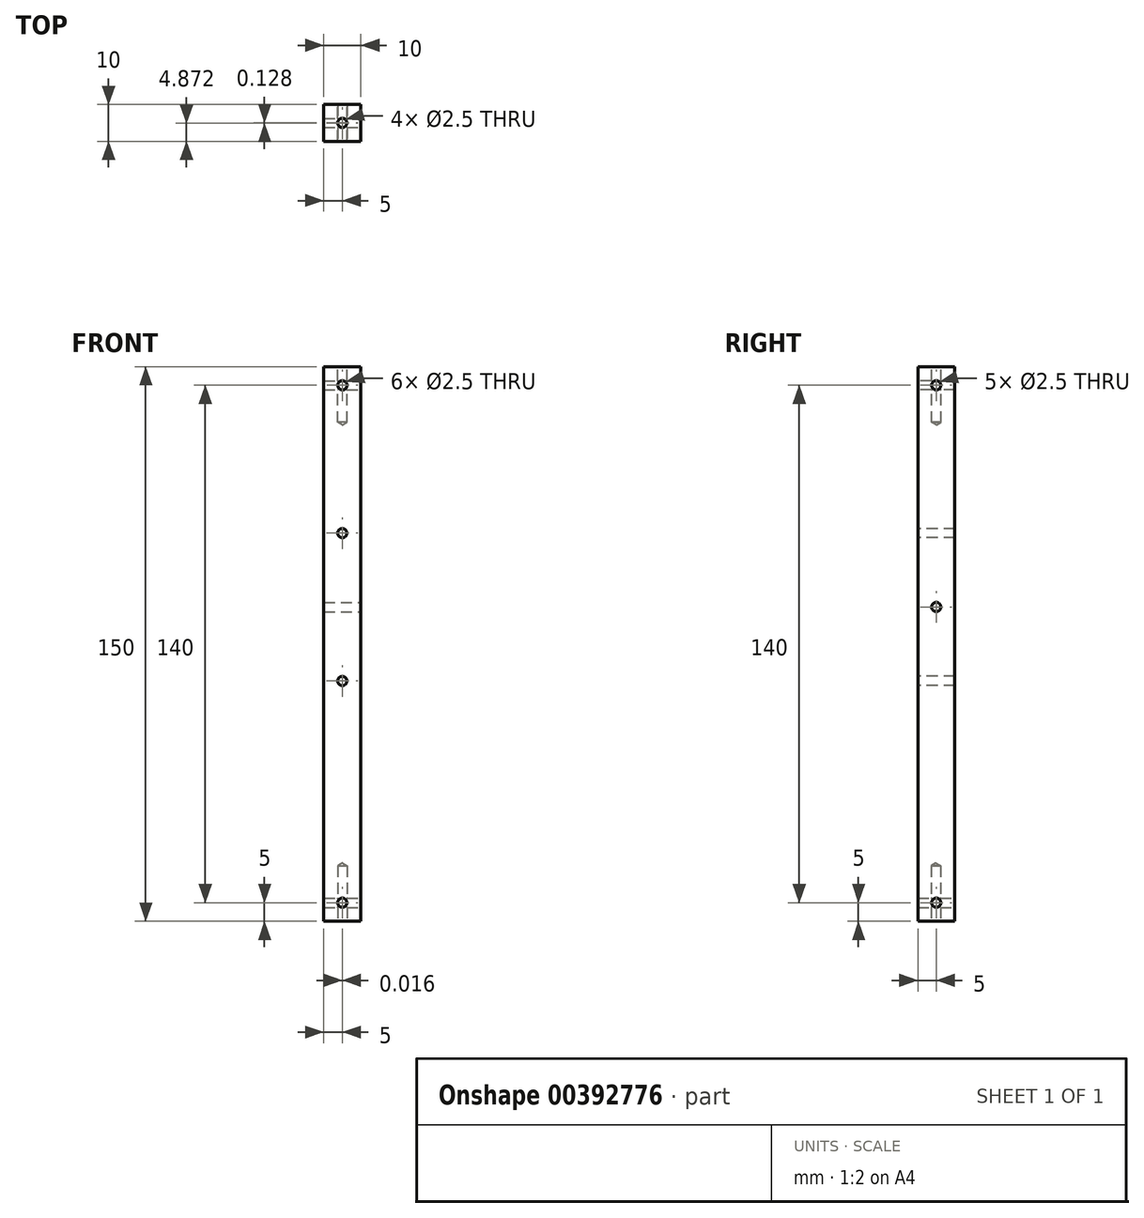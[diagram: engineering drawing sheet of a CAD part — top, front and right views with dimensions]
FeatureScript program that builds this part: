
annotation { "Feature Type Name" : "Feature", "Feature Type Description" : "" }
export const myFeature = defineFeature(function(context is Context, id is Id, definition is map)
    precondition{}
    {
        {
            var Q0;
            Q0=qCreatedBy(makeId("Top.planeOp"),FACE);
            var sketch = newSketch(context, id + "F0", { "sketchPlane" : qUnion([Q0])});
            skLineSegment(sketch, "E0.bottom", {"start": v(0, 0) * mm, "end": v(10, 0) * mm});
            skLineSegment(sketch, "E0.top", {"start": v(0, -10) * mm, "end": v(10, -10) * mm});
            skLineSegment(sketch, "E0.left", {"start": v(0, 0) * mm, "end": v(0, -10) * mm});
            skLineSegment(sketch, "E0.right", {"start": v(10, 0) * mm, "end": v(10, -10) * mm});
            skSolve(sketch);
        }
        {
            var Q0;
            Q0 = qSketchRegion(id + "F0", true);
            extrude(context, id + "F1", {"entities" : qUnion([Q0]), "depth" : 150 * mm});
        }
        {
            var Q0;
            Q0=makeQuery(id+"F1.opExtrude","CAP_FACE",FACE,{"disambiguationData":[OSD([sQuery(id+"F0.wireOp",EDGE,"E0.bottom"),sQuery(id+"F0.wireOp",EDGE,"E0.top"),sQuery(id+"F0.wireOp",EDGE,"E0.left"),sQuery(id+"F0.wireOp",EDGE,"E0.right")])],"isStart":false});
            var sketch = newSketch(context, id + "F2", { "sketchPlane" : qUnion([Q0])});
            skLineSegment(sketch, "E1.bottom", {"start": v(0, -10) * mm, "end": v(5, -10) * mm});
            skLineSegment(sketch, "E1.top", {"start": v(0, -5) * mm, "end": v(5, -5) * mm});
            skLineSegment(sketch, "E1.left", {"start": v(0, -10) * mm, "end": v(0, -5) * mm});
            skLineSegment(sketch, "E1.right", {"start": v(5, -10) * mm, "end": v(5, -5) * mm});
            skSolve(sketch);
        }
        {
            var Q0;
            Q0=sQuery(id+"F2.wireOp",VERTEX,"E1.top.end");
            var Q1;
            Q1=makeQuery(id+"F1.opExtrude","SWEPT_BODY",BODY,{"disambiguationData":[OSD([sQuery(id+"F0.wireOp",EDGE,"E0.bottom"),sQuery(id+"F0.wireOp",EDGE,"E0.top"),sQuery(id+"F0.wireOp",EDGE,"E0.left"),sQuery(id+"F0.wireOp",EDGE,"E0.right")])]});
            hole(context, id + "F3", {"style" : HoleStyle.SIMPLE, "endStyle" : HoleEndStyle.BLIND, "holeDiameter" : 2.5 * mm, "holeDepth" : 15 * mm, "isTappedThrough" : true, "tappedDepth" : 12 * mm, "tapClearance" : 3, "locations" : qUnion([Q0]), "scope" : qUnion([Q1])});
        }
        {
            var Q0;
            Q0=makeQuery(id+"F0.imprint","IMPRINT",FACE,{"disambiguationData":[TD([[makeQuery(id+"F0.imprint","IMPRINT",EDGE,{"derivedFrom":sQuery(id+"F0.wireOp",EDGE,"E0.bottom")}),-1.0]])]});
            var sketch = newSketch(context, id + "F4", { "sketchPlane" : qUnion([Q0])});
            skLineSegment(sketch, "E2.bottom", {"start": v(0, -10.13) * mm, "end": v(5, -10.13) * mm});
            skLineSegment(sketch, "E2.top", {"start": v(0, -5.13) * mm, "end": v(5, -5.13) * mm});
            skLineSegment(sketch, "E2.left", {"start": v(0, -10.13) * mm, "end": v(0, -5.13) * mm});
            skLineSegment(sketch, "E2.right", {"start": v(5, -10.13) * mm, "end": v(5, -5.13) * mm});
            skSolve(sketch);
        }
        {
            var Q0;
            Q0=sQuery(id+"F4.wireOp",VERTEX,"E2.right.end");
            var Q1;
            Q1=makeQuery(id+"F1.opExtrude","SWEPT_BODY",BODY,{"disambiguationData":[OSD([sQuery(id+"F0.wireOp",EDGE,"E0.bottom"),sQuery(id+"F0.wireOp",EDGE,"E0.top"),sQuery(id+"F0.wireOp",EDGE,"E0.left"),sQuery(id+"F0.wireOp",EDGE,"E0.right")])]});
            hole(context, id + "F5", {"style" : HoleStyle.SIMPLE, "endStyle" : HoleEndStyle.BLIND, "oppositeDirection" : true, "holeDiameter" : 2.5 * mm, "holeDepth" : 15 * mm, "isTappedThrough" : true, "tappedDepth" : 12 * mm, "tapClearance" : 3, "locations" : qUnion([Q0]), "scope" : qUnion([Q1])});
        }
        {
            var Q0;
            Q0=makeQuery(id+"F1.opExtrude","SWEPT_FACE",FACE,{"disambiguationData":[OSD([sQuery(id+"F0.wireOp",EDGE,"E0.bottom")])]});
            var sketch = newSketch(context, id + "F6", { "sketchPlane" : qUnion([Q0])});
            skLineSegment(sketch, "E3.bottom", {"start": v(-10, 0) * mm, "end": v(-5, 0) * mm});
            skLineSegment(sketch, "E3.top", {"start": v(-10, 5) * mm, "end": v(-5, 5) * mm});
            skLineSegment(sketch, "E3.left", {"start": v(-10, 0) * mm, "end": v(-10, 5) * mm});
            skLineSegment(sketch, "E3.right", {"start": v(-5, 0) * mm, "end": v(-5, 5) * mm});
            skSolve(sketch);
        }
        {
            var Q0;
            Q0=sQuery(id+"F6.wireOp",VERTEX,"E3.right.end");
            var Q1;
            Q1=makeQuery(id+"F1.opExtrude","SWEPT_BODY",BODY,{"disambiguationData":[OSD([sQuery(id+"F0.wireOp",EDGE,"E0.bottom"),sQuery(id+"F0.wireOp",EDGE,"E0.top"),sQuery(id+"F0.wireOp",EDGE,"E0.left"),sQuery(id+"F0.wireOp",EDGE,"E0.right")])]});
            hole(context, id + "F7", {"style" : HoleStyle.SIMPLE, "endStyle" : HoleEndStyle.BLIND, "holeDiameter" : 2.5 * mm, "holeDepth" : 10 * mm, "isTappedThrough" : true, "tappedDepth" : 12 * mm, "tapClearance" : 3, "locations" : qUnion([Q0]), "scope" : qUnion([Q1])});
        }
        {
            var Q0;
            Q0=makeQuery(id+"F1.opExtrude","SWEPT_FACE",FACE,{"disambiguationData":[OSD([sQuery(id+"F0.wireOp",EDGE,"E0.top")])]});
            var sketch = newSketch(context, id + "F8", { "sketchPlane" : qUnion([Q0])});
            skLineSegment(sketch, "E4.bottom", {"start": v(0, 150) * mm, "end": v(5.02, 150) * mm});
            skLineSegment(sketch, "E4.top", {"start": v(0, 145) * mm, "end": v(5.02, 145) * mm});
            skLineSegment(sketch, "E4.left", {"start": v(0, 150) * mm, "end": v(0, 145) * mm});
            skLineSegment(sketch, "E4.right", {"start": v(5.02, 150) * mm, "end": v(5.02, 145) * mm});
            skSolve(sketch);
        }
        {
            var Q0;
            Q0=sQuery(id+"F8.wireOp",VERTEX,"E4.right.end");
            var Q1;
            Q1=makeQuery(id+"F1.opExtrude","SWEPT_BODY",BODY,{"disambiguationData":[OSD([sQuery(id+"F0.wireOp",EDGE,"E0.bottom"),sQuery(id+"F0.wireOp",EDGE,"E0.top"),sQuery(id+"F0.wireOp",EDGE,"E0.left"),sQuery(id+"F0.wireOp",EDGE,"E0.right")])]});
            hole(context, id + "F9", {"style" : HoleStyle.SIMPLE, "endStyle" : HoleEndStyle.BLIND, "holeDiameter" : 2.5 * mm, "holeDepth" : 10 * mm, "isTappedThrough" : true, "tappedDepth" : 12 * mm, "tapClearance" : 3, "locations" : qUnion([Q0]), "scope" : qUnion([Q1])});
        }
        {
            var Q0;
            Q0=makeQuery(id+"F1.opExtrude","SWEPT_FACE",FACE,{"disambiguationData":[OSD([sQuery(id+"F0.wireOp",EDGE,"E0.top")])]});
            var sketch = newSketch(context, id + "F10", { "sketchPlane" : qUnion([Q0])});
            skPoint(sketch, "E5.oppositeSnap0", {"position": v(5, 0) * mm});
            skLineSegment(sketch, "E5.bottom", {"start": v(0, 0) * mm, "end": v(5, 0) * mm});
            skLineSegment(sketch, "E5.top", {"start": v(0, 65) * mm, "end": v(5, 65) * mm});
            skLineSegment(sketch, "E5.left", {"start": v(0, 0) * mm, "end": v(0, 65) * mm});
            skLineSegment(sketch, "E5.right", {"start": v(5, 0) * mm, "end": v(5, 65) * mm});
            skSolve(sketch);
        }
        {
            var Q0;
            Q0=sQuery(id+"F10.wireOp",VERTEX,"E5.top.end");
            var Q1;
            Q1=makeQuery(id+"F1.opExtrude","SWEPT_BODY",BODY,{"disambiguationData":[OSD([sQuery(id+"F0.wireOp",EDGE,"E0.bottom"),sQuery(id+"F0.wireOp",EDGE,"E0.top"),sQuery(id+"F0.wireOp",EDGE,"E0.left"),sQuery(id+"F0.wireOp",EDGE,"E0.right")])]});
            hole(context, id + "F11", {"style" : HoleStyle.SIMPLE, "endStyle" : HoleEndStyle.BLIND, "holeDiameter" : 2.5 * mm, "holeDepth" : 10 * mm, "isTappedThrough" : true, "tappedDepth" : 12 * mm, "tapClearance" : 3, "locations" : qUnion([Q0]), "scope" : qUnion([Q1])});
        }
        {
            var Q0;
            Q0=makeQuery(id+"F1.opExtrude","SWEPT_FACE",FACE,{"disambiguationData":[OSD([sQuery(id+"F0.wireOp",EDGE,"E0.top")])]});
            var sketch = newSketch(context, id + "F12", { "sketchPlane" : qUnion([Q0])});
            skLineSegment(sketch, "E6.bottom", {"start": v(5, 65) * mm, "end": v(10, 65) * mm});
            skLineSegment(sketch, "E6.top", {"start": v(5, 105) * mm, "end": v(10, 105) * mm});
            skLineSegment(sketch, "E6.left", {"start": v(5, 65) * mm, "end": v(5, 105) * mm});
            skLineSegment(sketch, "E6.right", {"start": v(10, 65) * mm, "end": v(10, 105) * mm});
            skSolve(sketch);
        }
        {
            var Q0;
            Q0=sQuery(id+"F12.wireOp",VERTEX,"E6.left.end");
            var Q1;
            Q1=makeQuery(id+"F1.opExtrude","SWEPT_BODY",BODY,{"disambiguationData":[OSD([sQuery(id+"F0.wireOp",EDGE,"E0.bottom"),sQuery(id+"F0.wireOp",EDGE,"E0.top"),sQuery(id+"F0.wireOp",EDGE,"E0.left"),sQuery(id+"F0.wireOp",EDGE,"E0.right")])]});
            hole(context, id + "F13", {"style" : HoleStyle.SIMPLE, "endStyle" : HoleEndStyle.BLIND, "holeDiameter" : 2.5 * mm, "holeDepth" : 10 * mm, "isTappedThrough" : true, "tappedDepth" : 12 * mm, "tapClearance" : 3, "locations" : qUnion([Q0]), "scope" : qUnion([Q1])});
        }
        {
            var Q0;
            Q0=makeQuery(id+"F1.opExtrude","SWEPT_FACE",FACE,{"disambiguationData":[OSD([sQuery(id+"F0.wireOp",EDGE,"E0.right")])]});
            var sketch = newSketch(context, id + "F14", { "sketchPlane" : qUnion([Q0])});
            skLineSegment(sketch, "E7.bottom", {"start": v(0, 150) * mm, "end": v(-5, 150) * mm});
            skLineSegment(sketch, "E7.top", {"start": v(0, 145) * mm, "end": v(-5, 145) * mm});
            skLineSegment(sketch, "E7.left", {"start": v(0, 150) * mm, "end": v(0, 145) * mm});
            skLineSegment(sketch, "E7.right", {"start": v(-5, 150) * mm, "end": v(-5, 145) * mm});
            skSolve(sketch);
        }
        {
            var Q0;
            Q0=sQuery(id+"F14.wireOp",VERTEX,"E7.right.end");
            var Q1;
            Q1=makeQuery(id+"F1.opExtrude","SWEPT_BODY",BODY,{"disambiguationData":[OSD([sQuery(id+"F0.wireOp",EDGE,"E0.bottom"),sQuery(id+"F0.wireOp",EDGE,"E0.top"),sQuery(id+"F0.wireOp",EDGE,"E0.left"),sQuery(id+"F0.wireOp",EDGE,"E0.right")])]});
            hole(context, id + "F15", {"style" : HoleStyle.SIMPLE, "endStyle" : HoleEndStyle.BLIND, "holeDiameter" : 2.5 * mm, "holeDepth" : 10 * mm, "isTappedThrough" : true, "tappedDepth" : 12 * mm, "tapClearance" : 3, "locations" : qUnion([Q0]), "scope" : qUnion([Q1])});
        }
        {
            var Q0;
            Q0=makeQuery(id+"F1.opExtrude","SWEPT_FACE",FACE,{"disambiguationData":[OSD([sQuery(id+"F0.wireOp",EDGE,"E0.right")])]});
            var sketch = newSketch(context, id + "F16", { "sketchPlane" : qUnion([Q0])});
            skLineSegment(sketch, "E8.bottom", {"start": v(-10, 0) * mm, "end": v(-5, 0) * mm});
            skLineSegment(sketch, "E8.top", {"start": v(-10, 5) * mm, "end": v(-5, 5) * mm});
            skLineSegment(sketch, "E8.left", {"start": v(-10, 0) * mm, "end": v(-10, 5) * mm});
            skLineSegment(sketch, "E8.right", {"start": v(-5, 0) * mm, "end": v(-5, 5) * mm});
            skSolve(sketch);
        }
        {
            var Q0;
            Q0=sQuery(id+"F16.wireOp",VERTEX,"E8.right.end");
            var Q1;
            Q1=makeQuery(id+"F1.opExtrude","SWEPT_BODY",BODY,{"disambiguationData":[OSD([sQuery(id+"F0.wireOp",EDGE,"E0.bottom"),sQuery(id+"F0.wireOp",EDGE,"E0.top"),sQuery(id+"F0.wireOp",EDGE,"E0.left"),sQuery(id+"F0.wireOp",EDGE,"E0.right")])]});
            hole(context, id + "F17", {"style" : HoleStyle.SIMPLE, "endStyle" : HoleEndStyle.BLIND, "holeDiameter" : 2.5 * mm, "holeDepth" : 10 * mm, "isTappedThrough" : true, "tappedDepth" : 12 * mm, "tapClearance" : 3, "locations" : qUnion([Q0]), "scope" : qUnion([Q1])});
        }
        {
            var Q0;
            Q0=makeQuery(id+"F1.opExtrude","SWEPT_FACE",FACE,{"disambiguationData":[OSD([sQuery(id+"F0.wireOp",EDGE,"E0.right")])]});
            var sketch = newSketch(context, id + "F18", { "sketchPlane" : qUnion([Q0])});
            skLineSegment(sketch, "E9.bottom", {"start": v(-10, 0) * mm, "end": v(-5, 0) * mm});
            skLineSegment(sketch, "E9.top", {"start": v(-10, 85) * mm, "end": v(-5, 85) * mm});
            skLineSegment(sketch, "E9.left", {"start": v(-10, 0) * mm, "end": v(-10, 85) * mm});
            skLineSegment(sketch, "E9.right", {"start": v(-5, 0) * mm, "end": v(-5, 85) * mm});
            skSolve(sketch);
        }
        {
            var Q0;
            Q0=sQuery(id+"F18.wireOp",VERTEX,"E9.right.end");
            var Q1;
            Q1=makeQuery(id+"F1.opExtrude","SWEPT_BODY",BODY,{"disambiguationData":[OSD([sQuery(id+"F0.wireOp",EDGE,"E0.bottom"),sQuery(id+"F0.wireOp",EDGE,"E0.top"),sQuery(id+"F0.wireOp",EDGE,"E0.left"),sQuery(id+"F0.wireOp",EDGE,"E0.right")])]});
            hole(context, id + "F19", {"style" : HoleStyle.SIMPLE, "endStyle" : HoleEndStyle.BLIND, "holeDiameter" : 2.5 * mm, "holeDepth" : 10 * mm, "isTappedThrough" : true, "tappedDepth" : 12 * mm, "tapClearance" : 3, "locations" : qUnion([Q0]), "scope" : qUnion([Q1])});
        }
    });
